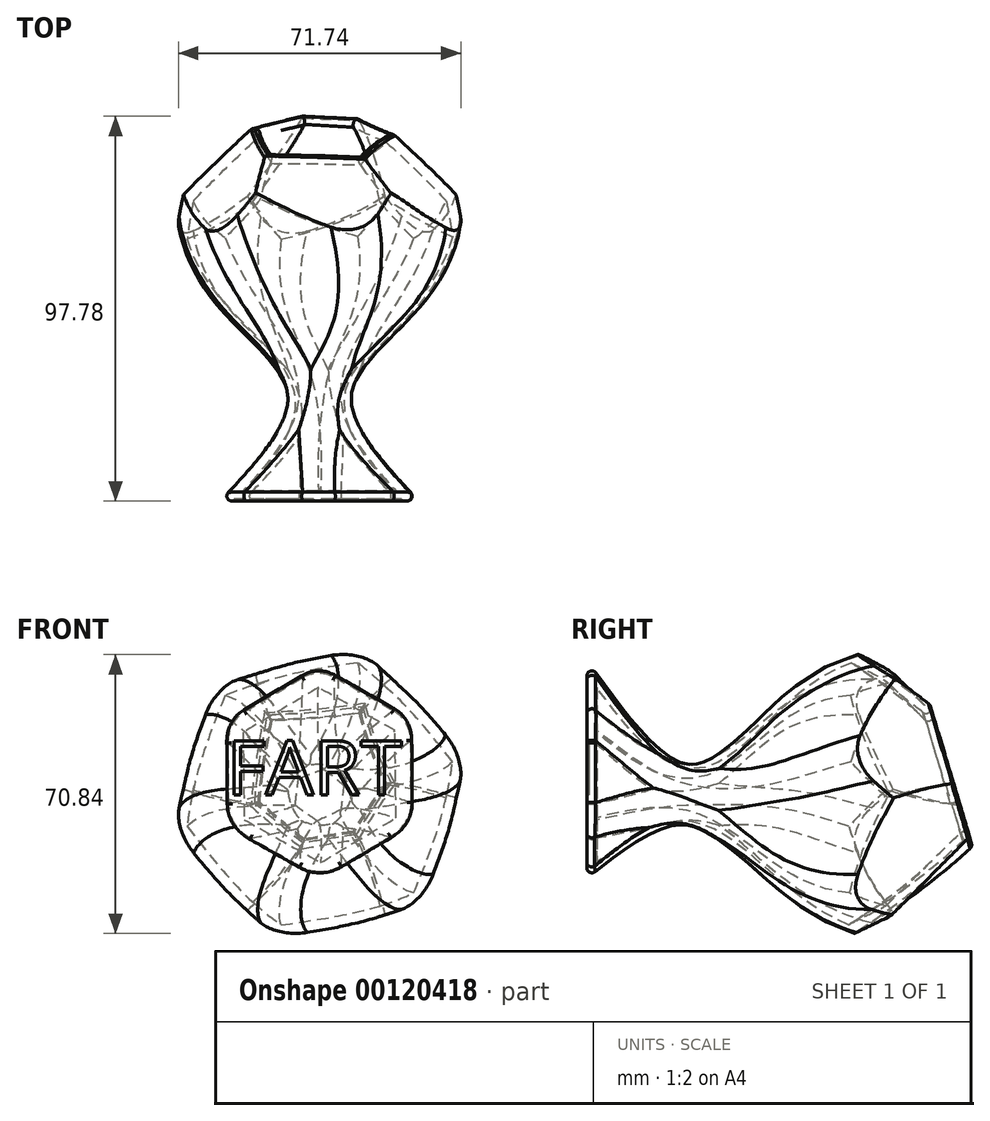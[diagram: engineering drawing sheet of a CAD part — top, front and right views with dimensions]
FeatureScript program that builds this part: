
annotation { "Feature Type Name" : "Feature", "Feature Type Description" : "" }
export const myFeature = defineFeature(function(context is Context, id is Id, definition is map)
    precondition{}
    {
        {
            var Q0;
            Q0=qCreatedBy(makeId("Front.planeOp"),FACE);
            cPlane(context, id + "F0", {"entities" : qUnion([Q0]), "cplaneType" : CPlaneType.OFFSET, "offset" : 25.4 * mm, "width" : 152.4 * mm, "height" : 152.4 * mm});
        }
        {
            var Q0;
            Q0=qCreatedBy(id+"F0.planeOp",FACE);
            cPlane(context, id + "F1", {"entities" : qUnion([Q0]), "cplaneType" : CPlaneType.OFFSET, "offset" : 25.4 * mm, "width" : 152.4 * mm, "height" : 152.4 * mm});
        }
        {
            var Q0;
            Q0=qCreatedBy(id+"F1.planeOp",FACE);
            cPlane(context, id + "F2", {"entities" : qUnion([Q0]), "cplaneType" : CPlaneType.OFFSET, "offset" : 25.4 * mm, "width" : 152.4 * mm, "height" : 152.4 * mm});
        }
        {
            var Q0;
            Q0=qCreatedBy(id+"F2.planeOp",FACE);
            cPlane(context, id + "F3", {"entities" : qUnion([Q0]), "cplaneType" : CPlaneType.OFFSET, "offset" : 25.4 * mm, "width" : 152.4 * mm, "height" : 152.4 * mm});
        }
        {
            var Q0;
            Q0=qCreatedBy(makeId("Front.planeOp"),FACE);
            var sketch = newSketch(context, id + "F4", { "sketchPlane" : qUnion([Q0])});
            skCircle(sketch, "E0.cCircle", {"center": v(0, 0) * mm, "radius": 28.9 * mm, "construction": true});
            skLineSegment(sketch, "E0.0", {"start": v(28.9, 16.69) * mm, "end": v(28.9, -16.69) * mm});
            skLineSegment(sketch, "E0.1", {"start": v(28.9, -16.69) * mm, "end": v(0, -33.38) * mm});
            skLineSegment(sketch, "E0.2", {"start": v(0, -33.38) * mm, "end": v(-28.9, -16.69) * mm});
            skLineSegment(sketch, "E0.3", {"start": v(-28.9, -16.69) * mm, "end": v(-28.9, 16.69) * mm});
            skLineSegment(sketch, "E0.4", {"start": v(-28.9, 16.69) * mm, "end": v(0, 33.38) * mm});
            skLineSegment(sketch, "E0.5", {"start": v(0, 33.38) * mm, "end": v(28.9, 16.69) * mm});
            skPoint(sketch, "E0.0.midPoint", {"position": v(28.9, 0) * mm});
            skSolve(sketch);
        }
        {
            var Q0;
            Q0=qCreatedBy(id+"F0.planeOp",FACE);
            var sketch = newSketch(context, id + "F5", { "sketchPlane" : qUnion([Q0])});
            skCircle(sketch, "E1.cCircle", {"center": v(0, 0) * mm, "radius": 34.1 * mm, "construction": true});
            skLineSegment(sketch, "E1.0", {"start": v(8.53, 38.44) * mm, "end": v(37.55, 11.83) * mm});
            skLineSegment(sketch, "E1.1", {"start": v(37.55, 11.83) * mm, "end": v(29.02, -26.6) * mm});
            skLineSegment(sketch, "E1.2", {"start": v(29.02, -26.6) * mm, "end": v(-8.53, -38.44) * mm});
            skLineSegment(sketch, "E1.3", {"start": v(-8.53, -38.44) * mm, "end": v(-37.55, -11.83) * mm});
            skLineSegment(sketch, "E1.4", {"start": v(-37.55, -11.83) * mm, "end": v(-29.02, 26.6) * mm});
            skLineSegment(sketch, "E1.5", {"start": v(-29.02, 26.6) * mm, "end": v(8.53, 38.44) * mm});
            skPoint(sketch, "E1.0.midPoint", {"position": v(23.04, 25.13) * mm});
            skSolve(sketch);
        }
        {
            var Q0;
            Q0=qCreatedBy(id+"F1.planeOp",FACE);
            var sketch = newSketch(context, id + "F6", { "sketchPlane" : qUnion([Q0])});
            skCircle(sketch, "E2.cCircle", {"center": v(0, 0) * mm, "radius": 24.73 * mm, "construction": true});
            skLineSegment(sketch, "E2.0", {"start": v(10.32, 26.62) * mm, "end": v(28.22, 4.37) * mm});
            skLineSegment(sketch, "E2.1", {"start": v(28.22, 4.37) * mm, "end": v(17.9, -22.25) * mm});
            skLineSegment(sketch, "E2.2", {"start": v(17.9, -22.25) * mm, "end": v(-10.32, -26.62) * mm});
            skLineSegment(sketch, "E2.3", {"start": v(-10.32, -26.62) * mm, "end": v(-28.22, -4.37) * mm});
            skLineSegment(sketch, "E2.4", {"start": v(-28.22, -4.37) * mm, "end": v(-17.9, 22.25) * mm});
            skLineSegment(sketch, "E2.5", {"start": v(-17.9, 22.25) * mm, "end": v(10.32, 26.62) * mm});
            skPoint(sketch, "E2.0.midPoint", {"position": v(19.27, 15.5) * mm});
            skSolve(sketch);
        }
        {
            var Q0;
            Q0=qCreatedBy(id+"F2.planeOp",FACE);
            var sketch = newSketch(context, id + "F7", { "sketchPlane" : qUnion([Q0])});
            skCircle(sketch, "E3.cCircle", {"center": v(0, 0) * mm, "radius": 8.38 * mm, "construction": true});
            skLineSegment(sketch, "E3.0", {"start": v(8.9, 3.82) * mm, "end": v(7.76, -5.8) * mm});
            skLineSegment(sketch, "E3.1", {"start": v(7.76, -5.8) * mm, "end": v(-1.14, -9.61) * mm});
            skLineSegment(sketch, "E3.2", {"start": v(-1.14, -9.61) * mm, "end": v(-8.9, -3.82) * mm});
            skLineSegment(sketch, "E3.3", {"start": v(-8.9, -3.82) * mm, "end": v(-7.76, 5.8) * mm});
            skLineSegment(sketch, "E3.4", {"start": v(-7.76, 5.8) * mm, "end": v(1.14, 9.61) * mm});
            skLineSegment(sketch, "E3.5", {"start": v(1.14, 9.61) * mm, "end": v(8.9, 3.82) * mm});
            skPoint(sketch, "E3.0.midPoint", {"position": v(8.32, -0.98) * mm});
            skSolve(sketch);
        }
        {
            var Q0;
            Q0=qCreatedBy(id+"F3.planeOp",FACE);
            var sketch = newSketch(context, id + "F8", { "sketchPlane" : qUnion([Q0])});
            skCircle(sketch, "E4.cCircle", {"center": v(0, 6.28) * mm, "radius": 25.17 * mm, "construction": true});
            skLineSegment(sketch, "E4.0", {"start": v(25.23, -8.14) * mm, "end": v(0.12, -22.78) * mm});
            skLineSegment(sketch, "E4.1", {"start": v(0.12, -22.78) * mm, "end": v(-25.11, -8.36) * mm});
            skLineSegment(sketch, "E4.2", {"start": v(-25.11, -8.36) * mm, "end": v(-25.23, 20.71) * mm});
            skLineSegment(sketch, "E4.3", {"start": v(-25.23, 20.71) * mm, "end": v(-0.12, 35.35) * mm});
            skLineSegment(sketch, "E4.4", {"start": v(-0.12, 35.35) * mm, "end": v(25.11, 20.92) * mm});
            skLineSegment(sketch, "E4.5", {"start": v(25.11, 20.92) * mm, "end": v(25.23, -8.14) * mm});
            skPoint(sketch, "E4.0.midPoint", {"position": v(12.68, -15.46) * mm});
            skSolve(sketch);
        }
        {
            var Q0;
            Q0=makeQuery(id+"F4.imprint","IMPRINT",FACE,{"disambiguationData":[TD([[makeQuery(id+"F4.imprint","IMPRINT",EDGE,{"derivedFrom":sQuery(id+"F4.wireOp",EDGE,"E0.0")}),-1.0]])]});
            var Q1;
            Q1=makeQuery(id+"F5.imprint","IMPRINT",FACE,{"disambiguationData":[TD([[makeQuery(id+"F5.imprint","IMPRINT",EDGE,{"derivedFrom":sQuery(id+"F5.wireOp",EDGE,"E1.0")}),-1.0]])]});
            var Q2;
            Q2=makeQuery(id+"F6.imprint","IMPRINT",FACE,{"disambiguationData":[TD([[makeQuery(id+"F6.imprint","IMPRINT",EDGE,{"derivedFrom":sQuery(id+"F6.wireOp",EDGE,"E2.0")}),-1.0]])]});
            var Q3;
            Q3=makeQuery(id+"F7.imprint","IMPRINT",FACE,{"disambiguationData":[TD([[makeQuery(id+"F7.imprint","IMPRINT",EDGE,{"derivedFrom":sQuery(id+"F7.wireOp",EDGE,"E3.0")}),-1.0]])]});
            var Q4;
            Q4=makeQuery(id+"F8.imprint","IMPRINT",FACE,{"disambiguationData":[TD([[makeQuery(id+"F8.imprint","IMPRINT",EDGE,{"derivedFrom":sQuery(id+"F8.wireOp",EDGE,"E4.0")}),-1.0]])]});
            loft(context, id + "F9", {"sheetProfilesArray" : [{ "sheetProfileEntities" : qUnion([Q0]) }, { "sheetProfileEntities" : qUnion([Q1]) }, { "sheetProfileEntities" : qUnion([Q2]) }, { "sheetProfileEntities" : qUnion([Q3]) }, { "sheetProfileEntities" : qUnion([Q4]) }]});
        }
        {
            var Q0;
            Q0=makeQuery(id+"F9.opLoft","CAP_FACE",FACE,{"disambiguationData":[OSD([makeQuery(id+"F4.imprint","IMPRINT",FACE,{"disambiguationData":[TD([[makeQuery(id+"F4.imprint","IMPRINT",EDGE,{"derivedFrom":sQuery(id+"F4.wireOp",EDGE,"E0.0")}),-1.0]])]})])],"isStart":true});
            chamfer(context, id + "F10", {"entities" : qUnion([Q0]), "width" : 25.4 * mm, "tangentPropagation" : true});
        }
        {
            var Q0;
            Q0=makeQuery(id+"F9.opLoft","CAP_FACE",FACE,{"disambiguationData":[OSD([makeQuery(id+"F4.imprint","IMPRINT",FACE,{"disambiguationData":[TD([[makeQuery(id+"F4.imprint","IMPRINT",EDGE,{"derivedFrom":sQuery(id+"F4.wireOp",EDGE,"E0.0")}),-1.0]])]})])],"isStart":true});
            shell(context, id + "F11", {"entities" : qUnion([Q0]), "thickness" : 2.54 * mm});
        }
        {
            var Q0;
            Q0=qCreatedBy(makeId("Right.planeOp"),FACE);
            var sketch = newSketch(context, id + "F12", { "sketchPlane" : qUnion([Q0])});
            skLineSegment(sketch, "E5", {"start": v(0, -25.21) * mm, "end": v(-18.3, 35.78) * mm});
            skLineSegment(sketch, "E6", {"start": v(-18.3, 35.78) * mm, "end": v(32.58, 29.05) * mm});
            skLineSegment(sketch, "E7", {"start": v(32.58, 29.05) * mm, "end": v(0, -25.21) * mm});
            skSolve(sketch);
        }
        {
            var Q0;
            Q0=makeQuery(id+"F12.imprint","IMPRINT",FACE,{"disambiguationData":[TD([[makeQuery(id+"F12.imprint","IMPRINT",EDGE,{"derivedFrom":sQuery(id+"F12.wireOp",EDGE,"E5")}),-1.0]])]});
            extrude(context, id + "F13", {"entities" : qUnion([Q0]), "operationType" : NewBodyOperationType.REMOVE, "endBound" : BoundingType.THROUGH_ALL, "oppositeDirection" : true, "depth" : 25.4 * mm, "hasSecondDirection" : true, "secondDirectionBound" : SecondDirectionBoundingType.THROUGH_ALL, "secondDirectionOppositeDirection" : false, "secondDirectionDepth" : 25.4 * mm});
        }
        {
            var Q0;
            Q0=makeQuery(id+"F13.boolean.opBoolean","COPY",FACE,{"derivedFrom":makeQuery(id+"F13.opExtrude","SWEPT_FACE",FACE,{"disambiguationData":[OSD([sQuery(id+"F12.wireOp",EDGE,"E5")])]})});
            fillet(context, id + "F14", {"entities" : qUnion([Q0]), "radius" : 1.27 * mm, "tangentPropagation" : true, "allowEdgeOverflow" : false});
        }
        {
            var Q0;
            Q0=makeQuery(id+"F9.opLoft","SWEPT_EDGE",EDGE,{"disambiguationData":[OSD([sQuery(id+"F4.wireOp",EDGE,"E0.0"),sQuery(id+"F4.wireOp",EDGE,"E0.1"),sQuery(id+"F5.wireOp",EDGE,"E1.1"),sQuery(id+"F5.wireOp",EDGE,"E1.2")])]});
            var Q1;
            Q1=makeQuery(id+"F9.opLoft","SWEPT_EDGE",EDGE,{"disambiguationData":[OSD([sQuery(id+"F4.wireOp",EDGE,"E0.0"),sQuery(id+"F4.wireOp",EDGE,"E0.5"),sQuery(id+"F5.wireOp",EDGE,"E1.0"),sQuery(id+"F5.wireOp",EDGE,"E1.1")])]});
            var Q2;
            Q2=makeQuery(id+"F9.opLoft","SWEPT_EDGE",EDGE,{"disambiguationData":[OSD([sQuery(id+"F4.wireOp",EDGE,"E0.1"),sQuery(id+"F4.wireOp",EDGE,"E0.2"),sQuery(id+"F5.wireOp",EDGE,"E1.2"),sQuery(id+"F5.wireOp",EDGE,"E1.3")])]});
            var Q3;
            Q3=makeQuery(id+"F9.opLoft","SWEPT_EDGE",EDGE,{"disambiguationData":[OSD([sQuery(id+"F4.wireOp",EDGE,"E0.2"),sQuery(id+"F4.wireOp",EDGE,"E0.3"),sQuery(id+"F5.wireOp",EDGE,"E1.3"),sQuery(id+"F5.wireOp",EDGE,"E1.4")])]});
            var Q4;
            Q4=makeQuery(id+"F9.opLoft","SWEPT_EDGE",EDGE,{"disambiguationData":[OSD([sQuery(id+"F4.wireOp",EDGE,"E0.3"),sQuery(id+"F4.wireOp",EDGE,"E0.4"),sQuery(id+"F5.wireOp",EDGE,"E1.4"),sQuery(id+"F5.wireOp",EDGE,"E1.5")])]});
            var Q5;
            Q5=makeQuery(id+"F9.opLoft","SWEPT_EDGE",EDGE,{"disambiguationData":[OSD([sQuery(id+"F4.wireOp",EDGE,"E0.4"),sQuery(id+"F4.wireOp",EDGE,"E0.5"),sQuery(id+"F5.wireOp",EDGE,"E1.0"),sQuery(id+"F5.wireOp",EDGE,"E1.5")])]});
            fillet(context, id + "F15", {"entities" : qUnion([Q0, Q1, Q2, Q3, Q4, Q5]), "radius" : 12.7 * mm, "tangentPropagation" : true, "allowEdgeOverflow" : false});
        }
        {
            var Q0;
            Q0=makeQuery(id+"F9.opLoft","CAP_FACE",FACE,{"disambiguationData":[OSD([makeQuery(id+"F8.imprint","IMPRINT",FACE,{"disambiguationData":[TD([[makeQuery(id+"F8.imprint","IMPRINT",EDGE,{"derivedFrom":sQuery(id+"F8.wireOp",EDGE,"E4.0")}),-1.0]])]})])],"isStart":true});
            fillet(context, id + "F16", {"entities" : qUnion([Q0]), "radius" : 1.27 * mm, "tangentPropagation" : true, "allowEdgeOverflow" : false});
        }
        {
            var Q0;
            Q0=makeQuery(id+"F9.opLoft","CAP_FACE",FACE,{"disambiguationData":[OSD([makeQuery(id+"F8.imprint","IMPRINT",FACE,{"disambiguationData":[TD([[makeQuery(id+"F8.imprint","IMPRINT",EDGE,{"derivedFrom":sQuery(id+"F8.wireOp",EDGE,"E4.0")}),-1.0]])]})])],"isStart":true});
            var sketch = newSketch(context, id + "F17", { "sketchPlane" : qUnion([Q0])});
            skText(sketch, "E8", { "text": "FART", "fontName": "OpenSans-Regular.ttf"});
            const initialGuessF17  = {"E8": [-0.02358, 0, 1, 0, 0.01385]};
            skSetInitialGuess(sketch, initialGuessF17);
            skSolve(sketch);
        }
        {
            var Q0;
            Q0 = qSketchRegion(id + "F17", true);
            extrude(context, id + "F18", {"entities" : qUnion([Q0]), "operationType" : NewBodyOperationType.REMOVE, "oppositeDirection" : true, "depth" : 0.5 * mm});
        }
    });
